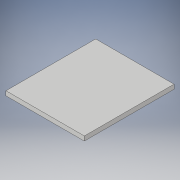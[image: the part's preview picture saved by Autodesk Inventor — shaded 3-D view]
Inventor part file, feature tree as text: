
AUTODESK INVENTOR PART (.ipt)
format: ipt  version: 2019 (Build 230136000, 136)  size: 90,624 bytes
history: native  units: mm
features: extrude x1, sketch x1
ambient origin geometry x8: Origin, YZ Plane, XZ Plane, XY Plane, X Axis, Y Axis, Z Axis, Center Point
bodies: Solid1 (feature_tree)
feature tree (2):
  extrude  "Extrusion1"  Depth=56.36mm
  sketch  "Sketch1"  dims[d0=64.54mm d1=56.36mm d2=3.18mm d3=0.0mm]
